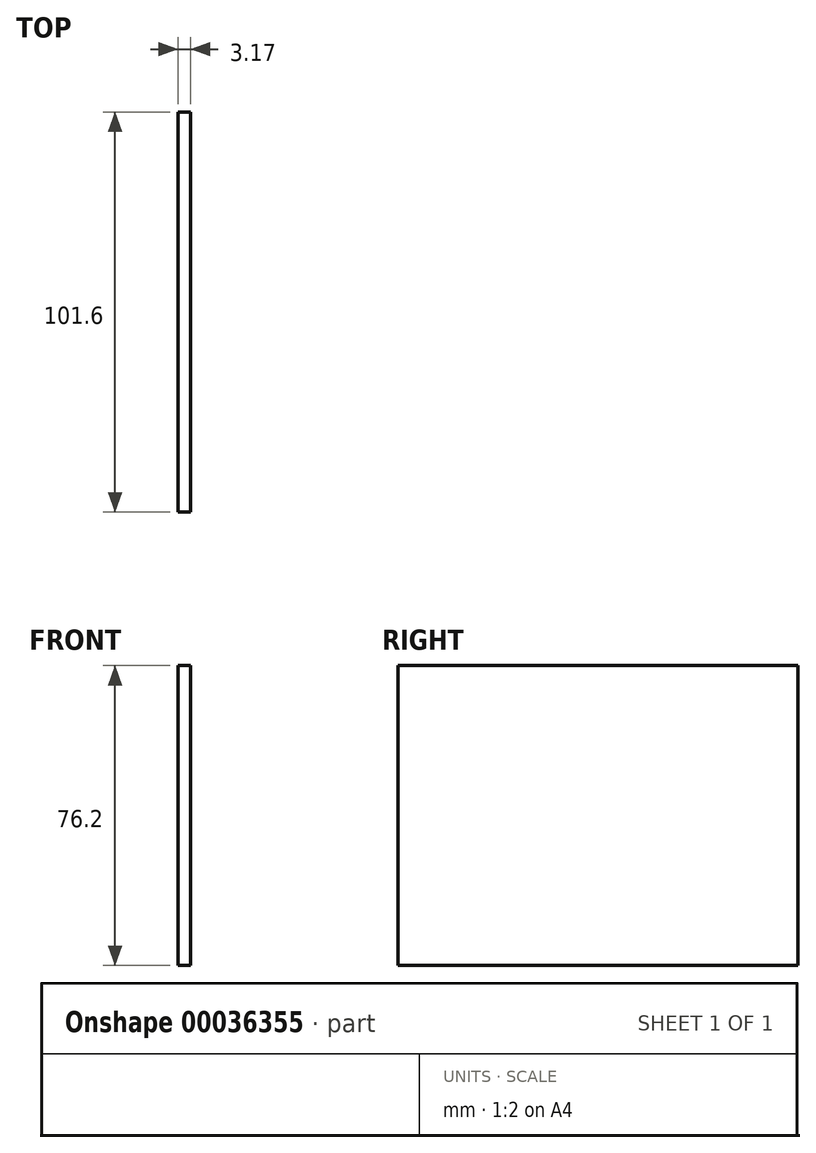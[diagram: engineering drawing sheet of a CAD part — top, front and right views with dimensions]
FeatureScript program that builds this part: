
annotation { "Feature Type Name" : "Feature", "Feature Type Description" : "" }
export const myFeature = defineFeature(function(context is Context, id is Id, definition is map)
    precondition{}
    {
        {
            var Q0;
            Q0=qCreatedBy(makeId("Right.planeOp"),FACE);
            var sketch = newSketch(context, id + "F0", { "sketchPlane" : qUnion([Q0])});
            skLineSegment(sketch, "E0.rect.bottom", {"start": v(-50.8, 38.1) * mm, "end": v(50.8, 38.1) * mm});
            skLineSegment(sketch, "E0.rect.top", {"start": v(-50.8, -38.1) * mm, "end": v(50.8, -38.1) * mm});
            skLineSegment(sketch, "E0.rect.left", {"start": v(-50.8, 38.1) * mm, "end": v(-50.8, -38.1) * mm});
            skLineSegment(sketch, "E0.rect.right", {"start": v(50.8, 38.1) * mm, "end": v(50.8, -38.1) * mm});
            skPoint(sketch, "E0.rect.middle", {"position": v(0, 0) * mm});
            skSolve(sketch);
        }
        {
            var Q0;
            Q0=makeQuery(id+"F0.imprint","IMPRINT",FACE,{"disambiguationData":[TD([[makeQuery(id+"F0.imprint","IMPRINT",EDGE,{"derivedFrom":sQuery(id+"F0.wireOp",EDGE,"E0.rect.bottom")}),-1.0]])]});
            extrude(context, id + "F1", {"entities" : qUnion([Q0]), "depth" : 3.17 * mm});
        }
    });
